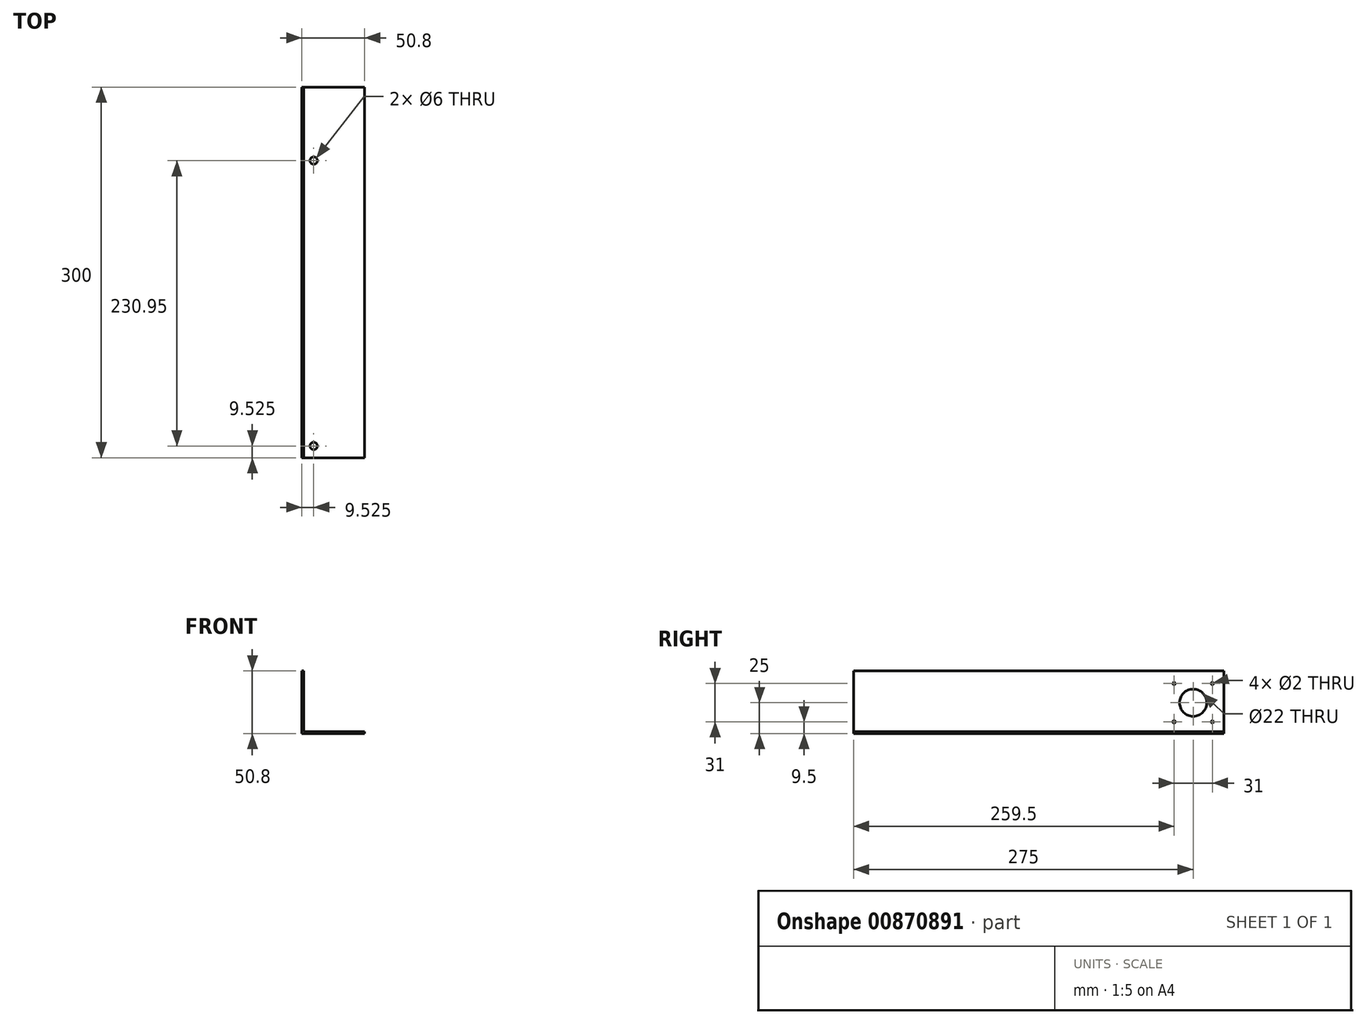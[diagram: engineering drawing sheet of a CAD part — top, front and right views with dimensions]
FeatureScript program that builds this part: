
annotation { "Feature Type Name" : "Feature", "Feature Type Description" : "" }
export const myFeature = defineFeature(function(context is Context, id is Id, definition is map)
    precondition{}
    {
        {
            var Q0;
            Q0=qCreatedBy(makeId("Front.planeOp"),FACE);
            var sketch = newSketch(context, id + "F0", { "sketchPlane" : qUnion([Q0])});
            skLineSegment(sketch, "E0", {"start": v(0, 0) * mm, "end": v(0, 50.8) * mm});
            skLineSegment(sketch, "E1", {"start": v(0, 50.8) * mm, "end": v(1.59, 50.8) * mm});
            skLineSegment(sketch, "E2", {"start": v(1.59, 50.8) * mm, "end": v(1.6, 1.59) * mm});
            skLineSegment(sketch, "E3", {"start": v(1.6, 1.59) * mm, "end": v(50.8, 1.6) * mm});
            skLineSegment(sketch, "E4", {"start": v(50.8, 1.6) * mm, "end": v(50.8, 0) * mm});
            skLineSegment(sketch, "E5", {"start": v(50.8, 0) * mm, "end": v(0, 0) * mm});
            skSolve(sketch);
        }
        {
            var Q0;
            Q0=qSketchRegion(id+"F0",true);
            extrude(context, id + "F1", {"entities" : qUnion([Q0]), "depth" : 300 * mm, "offsetDistance" : 25 * mm});
        }
        {
            var Q0;
            Q0=qCreatedBy(makeId("Top.planeOp"),FACE);
            var sketch = newSketch(context, id + "F2", { "sketchPlane" : qUnion([Q0])});
            skPoint(sketch, "E6", {"position": v(9.53, -59.52) * mm});
            skPoint(sketch, "E7", {"position": v(9.53, -290.48) * mm});
            skCircle(sketch, "E8", {"center": v(9.53, -59.52) * mm, "radius": 3 * mm});
            skCircle(sketch, "E9", {"center": v(9.53, -290.48) * mm, "radius": 3 * mm});
            skSolve(sketch);
        }
        {
            var Q0;
            Q0=qSketchRegion(id+"F2",true);
            extrude(context, id + "F3", {"entities" : qUnion([Q0]), "operationType" : NewBodyOperationType.REMOVE, "endBound" : BoundingType.THROUGH_ALL, "depth" : 25 * mm, "offsetDistance" : 25 * mm});
        }
        {
            var Q0;
            Q0=qCreatedBy(makeId("Right.planeOp"),FACE);
            var sketch = newSketch(context, id + "F4", { "sketchPlane" : qUnion([Q0])});
            skPoint(sketch, "E10", {"position": v(-25, 25) * mm});
            skCircle(sketch, "E11", {"center": v(-25, 25) * mm, "radius": 11 * mm});
            skPoint(sketch, "E12", {"position": v(-9.5, 9.5) * mm});
            skPoint(sketch, "E13", {"position": v(-40.5, 9.5) * mm});
            skPoint(sketch, "E14", {"position": v(-40.5, 40.5) * mm});
            skPoint(sketch, "E15", {"position": v(-9.5, 40.5) * mm});
            skCircle(sketch, "E16", {"center": v(-40.5, 9.5) * mm, "radius": 1 * mm});
            skCircle(sketch, "E17", {"center": v(-9.5, 9.5) * mm, "radius": 1 * mm});
            skCircle(sketch, "E18", {"center": v(-9.5, 40.5) * mm, "radius": 1 * mm});
            skCircle(sketch, "E19", {"center": v(-40.5, 40.5) * mm, "radius": 1 * mm});
            skSolve(sketch);
        }
        {
            var Q0;
            Q0 = qSketchRegion(id + "F4", true);
            extrude(context, id + "F5", {"entities" : qUnion([Q0]), "operationType" : NewBodyOperationType.REMOVE, "endBound" : BoundingType.THROUGH_ALL, "depth" : 25 * mm, "offsetDistance" : 25 * mm});
        }
    });
